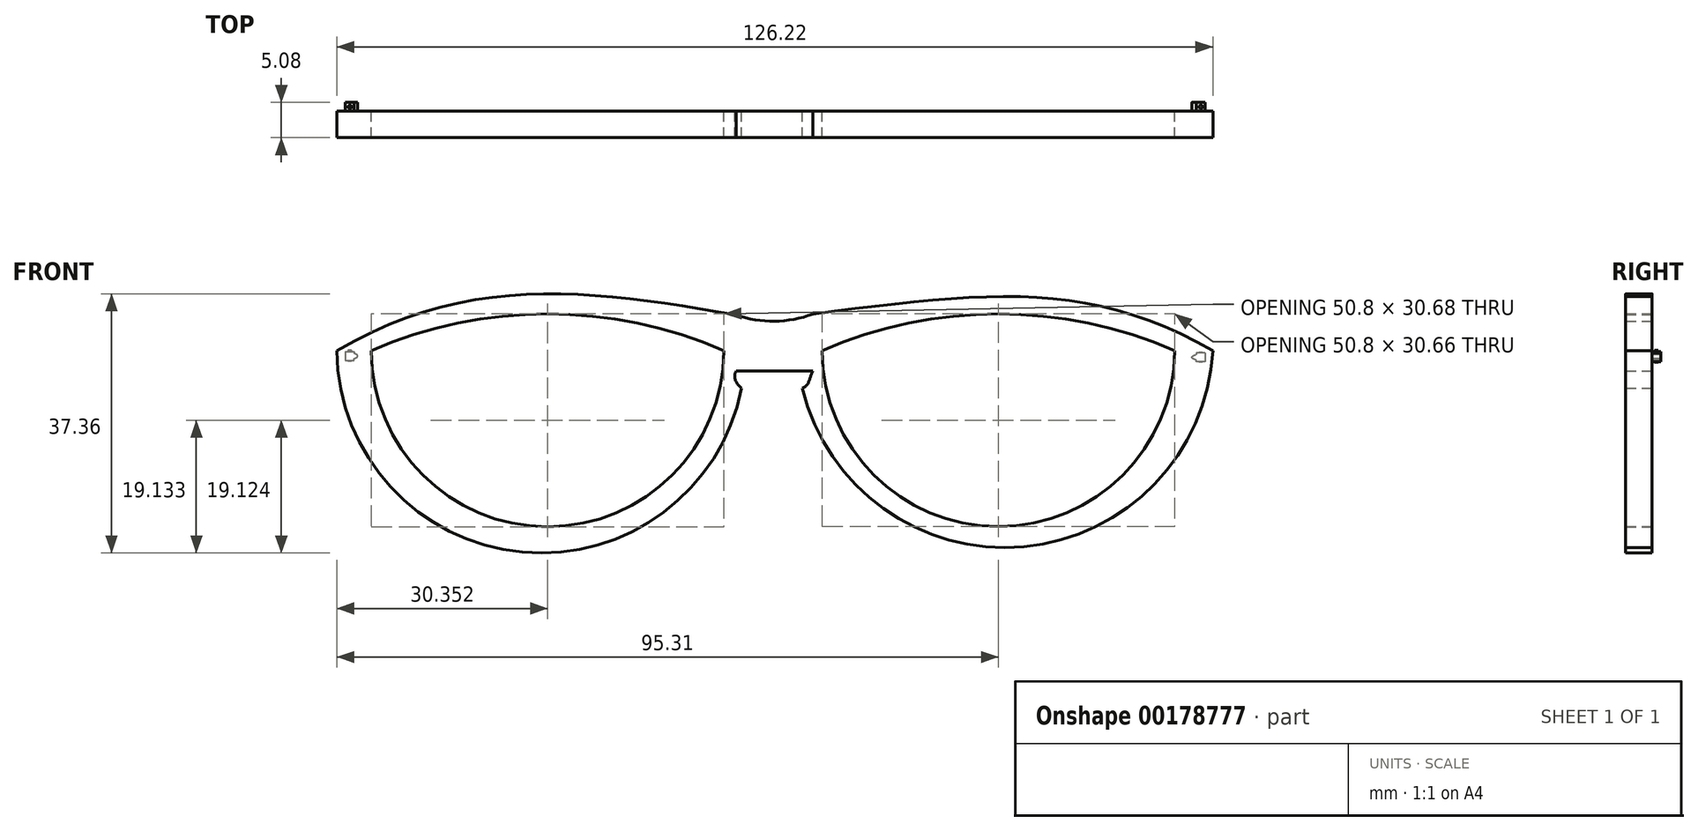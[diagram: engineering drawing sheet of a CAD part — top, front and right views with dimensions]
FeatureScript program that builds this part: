
annotation { "Feature Type Name" : "Feature", "Feature Type Description" : "" }
export const myFeature = defineFeature(function(context is Context, id is Id, definition is map)
    precondition{}
    {
        {
            var Q0;
            Q0=qCreatedBy(makeId("Front.planeOp"),FACE);
            var sketch = newSketch(context, id + "F0", { "sketchPlane" : qUnion([Q0])});
            skArc(sketch, "E0", {"start": v(-58.02, 0) * mm, "mid": v(-32.62, -25.37) * mm, "end": v(-7.22, 0) * mm});
            skArc(sketch, "E1", {"start": v(6.94, 0) * mm, "mid": v(32.34, -25.36) * mm, "end": v(57.74, 0) * mm});
            skArc(sketch, "E2", {"start": v(-7.22, 0) * mm, "mid": v(-32.62, 5.3) * mm, "end": v(-58.02, 0) * mm});
            skArc(sketch, "E3", {"start": v(57.74, 0) * mm, "mid": v(32.34, 5.3) * mm, "end": v(6.94, 0) * mm});
            skArc(sketch, "E4", {"start": v(-62.97, 0) * mm, "mid": v(-36.25, -29.04) * mm, "end": v(-4.66, -5.4) * mm});
            skArc(sketch, "E5", {"start": v(4.08, -5.4) * mm, "mid": v(36, -28.25) * mm, "end": v(63.25, 0) * mm});
            skLineSegment(sketch, "E6", {"start": v(-5.44, -2.93) * mm, "end": v(5.6, -2.93) * mm});
            skFitSpline(sketch, "E7", {"points": [v(-4.66, -5.4) * mm, v(-5.44, -2.93) * mm], "startDerivative": vector(-2.72, 1.99) * mm, "endDerivative": vector(1.48, 2.16) * mm});
            skFitSpline(sketch, "E8", {"points": [v(4.08, -5.4) * mm, v(5.6, -2.93) * mm], "startDerivative": vector(3.37, 1.04) * mm, "endDerivative": vector(1.53, 2.46) * mm});
            skArc(sketch, "E9", {"start": v(-5.44, 5.17) * mm, "mid": v(0.1, 4.25) * mm, "end": v(5.6, 5.29) * mm});
            skFitSpline(sketch, "E10", {"points": [v(-62.97, 0) * mm, v(-5.44, 5.17) * mm], "startDerivative": vector(58.46, 34.46) * mm, "endDerivative": vector(60.07, -10.18) * mm});
            skFitSpline(sketch, "E11", {"points": [v(63.25, 0) * mm, v(5.6, 5.29) * mm], "startDerivative": vector(-54.18, 31.35) * mm, "endDerivative": vector(-72.24, -9.35) * mm});
            skSolve(sketch);
        }
        {
            var Q0;
            Q0=makeQuery(id+"F0.imprint","IMPRINT",FACE,{"disambiguationData":[TD([[makeQuery(id+"F0.imprint","IMPRINT",EDGE,{"derivedFrom":sQuery(id+"F0.wireOp",EDGE,"E0")}),-1.0]])]});
            extrude(context, id + "F1", {"entities" : qUnion([Q0]), "depth" : 3.8 * mm});
        }
        {
            var Q0;
            Q0=makeQuery(id+"F1.opExtrude","CAP_FACE",FACE,{"disambiguationData":[OSD([sQuery(id+"F0.wireOp",EDGE,"E0"),sQuery(id+"F0.wireOp",EDGE,"E1"),sQuery(id+"F0.wireOp",EDGE,"E2"),sQuery(id+"F0.wireOp",EDGE,"E3"),sQuery(id+"F0.wireOp",EDGE,"E4"),sQuery(id+"F0.wireOp",EDGE,"E5"),sQuery(id+"F0.wireOp",EDGE,"E6"),sQuery(id+"F0.wireOp",EDGE,"E7"),sQuery(id+"F0.wireOp",EDGE,"E8"),sQuery(id+"F0.wireOp",EDGE,"E9"),sQuery(id+"F0.wireOp",EDGE,"E10"),sQuery(id+"F0.wireOp",EDGE,"E11")])],"isStart":true});
            var sketch = newSketch(context, id + "F2", { "sketchPlane" : qUnion([Q0])});
            skLineSegment(sketch, "E12", {"start": v(61.74, -0.13) * mm, "end": v(61.74, -1.4) * mm});
            skLineSegment(sketch, "E13", {"start": v(61.74, -1.4) * mm, "end": v(60.47, -1.4) * mm});
            skLineSegment(sketch, "E14", {"start": v(61.74, -0.13) * mm, "end": v(60.47, -0.13) * mm});
            skLineSegment(sketch, "E15", {"start": v(60.47, -1.4) * mm, "end": v(60.47, -1.15) * mm});
            skLineSegment(sketch, "E16", {"start": v(60.47, -0.13) * mm, "end": v(60.47, -0.38) * mm});
            skFitSpline(sketch, "E17", {"points": [v(60.47, -1.15) * mm, v(60.47, -0.38) * mm], "startDerivative": vector(-2.07, 0.8) * mm, "endDerivative": vector(2.02, 0.8) * mm});
            skSolve(sketch);
        }
        {
            var Q0;
            Q0=makeQuery(id+"F2.imprint","IMPRINT",FACE,{"disambiguationData":[TD([[makeQuery(id+"F2.imprint","IMPRINT",EDGE,{"derivedFrom":sQuery(id+"F2.wireOp",EDGE,"E12")}),-1.0]])]});
            extrude(context, id + "F3", {"entities" : qUnion([Q0]), "operationType" : NewBodyOperationType.ADD, "depth" : 1.27 * mm});
        }
        {
            var Q0;
            Q0=qCreatedBy(makeId("Top.planeOp"),FACE);
            var sketch = newSketch(context, id + "F4", { "sketchPlane" : qUnion([Q0])});
            skCircle(sketch, "E18", {"center": v(-61.1, 0.64) * mm, "radius": 0.25 * mm});
            skSolve(sketch);
        }
        {
            var Q0;
            Q0 = qSketchRegion(id + "F4", true);
            extrude(context, id + "F5", {"entities" : qUnion([Q0]), "depth" : 0.05 * mm});
        }
        {
            var Q0;
            Q0=makeQuery(id+"F3.opExtrude","SWEPT_FACE",FACE,{"disambiguationData":[OSD([sQuery(id+"F2.wireOp",EDGE,"E13")])]});
            var sketch = newSketch(context, id + "F6", { "sketchPlane" : qUnion([Q0])});
            skCircle(sketch, "E19", {"center": v(-61.1, -0.64) * mm, "radius": 0.25 * mm});
            skSolve(sketch);
        }
        {
            var Q0;
            Q0 = qSketchRegion(id + "F6", true);
            extrude(context, id + "F7", {"entities" : qUnion([Q0]), "operationType" : NewBodyOperationType.ADD, "depth" : 0.05 * mm});
        }
        {
            var Q0;
            Q0=makeQuery(id+"F1.opExtrude","CAP_FACE",FACE,{"disambiguationData":[OSD([sQuery(id+"F0.wireOp",EDGE,"E0"),sQuery(id+"F0.wireOp",EDGE,"E1"),sQuery(id+"F0.wireOp",EDGE,"E2"),sQuery(id+"F0.wireOp",EDGE,"E3"),sQuery(id+"F0.wireOp",EDGE,"E4"),sQuery(id+"F0.wireOp",EDGE,"E5"),sQuery(id+"F0.wireOp",EDGE,"E6"),sQuery(id+"F0.wireOp",EDGE,"E7"),sQuery(id+"F0.wireOp",EDGE,"E8"),sQuery(id+"F0.wireOp",EDGE,"E9"),sQuery(id+"F0.wireOp",EDGE,"E10"),sQuery(id+"F0.wireOp",EDGE,"E11")])],"isStart":true});
            var sketch = newSketch(context, id + "F8", { "sketchPlane" : qUnion([Q0])});
            skSolve(sketch);
        }
        {
            var Q0;
            Q0=makeQuery(id+"F8.imprint","IMPRINT",FACE,{"disambiguationData":[TD([[makeQuery(id+"F8.imprint","IMPRINT",EDGE,{"derivedFrom":makeQuery(id+"F1.opExtrude","CAP_EDGE",EDGE,{"disambiguationData":[OSD([sQuery(id+"F0.wireOp",EDGE,"E0")])],"isStart":true})}),1.0]])]});
            var sketch = newSketch(context, id + "F9", { "sketchPlane" : qUnion([Q0])});
            skLineSegment(sketch, "E20", {"start": v(-62.14, -0.32) * mm, "end": v(-60.87, -0.32) * mm});
            skLineSegment(sketch, "E21", {"start": v(-62.14, -0.32) * mm, "end": v(-62.14, -1.6) * mm});
            skLineSegment(sketch, "E22", {"start": v(-62.14, -1.6) * mm, "end": v(-60.87, -1.6) * mm});
            skLineSegment(sketch, "E23", {"start": v(-60.87, -1.6) * mm, "end": v(-60.87, -1.34) * mm});
            skLineSegment(sketch, "E24", {"start": v(-60.87, -0.32) * mm, "end": v(-60.87, -0.58) * mm});
            skFitSpline(sketch, "E25", {"points": [v(-60.87, -1.34) * mm, v(-60.87, -0.58) * mm], "startDerivative": vector(2.46, 0.55) * mm, "endDerivative": vector(-2.8, 0.69) * mm});
            skSolve(sketch);
        }
        {
            var Q0;
            Q0 = qSketchRegion(id + "F9", true);
            extrude(context, id + "F10", {"entities" : qUnion([Q0]), "operationType" : NewBodyOperationType.ADD, "depth" : 1.27 * mm});
        }
        {
            var Q0;
            Q0=makeQuery(id+"F10.opExtrude","SWEPT_FACE",FACE,{"disambiguationData":[OSD([sQuery(id+"F9.wireOp",EDGE,"E22")])]});
            var sketch = newSketch(context, id + "F11", { "sketchPlane" : qUnion([Q0])});
            skCircle(sketch, "E26", {"center": v(61.5, -0.64) * mm, "radius": 0.25 * mm});
            skSolve(sketch);
        }
        {
            var Q0;
            Q0 = qSketchRegion(id + "F11", true);
            extrude(context, id + "F12", {"entities" : qUnion([Q0]), "operationType" : NewBodyOperationType.ADD, "depth" : 0.05 * mm});
        }
        {
            var Q0;
            Q0=makeQuery(id+"F10.opExtrude","SWEPT_FACE",FACE,{"disambiguationData":[OSD([sQuery(id+"F9.wireOp",EDGE,"E20")])]});
            var sketch = newSketch(context, id + "F13", { "sketchPlane" : qUnion([Q0])});
            skCircle(sketch, "E27", {"center": v(61.5, 0.64) * mm, "radius": 0.25 * mm});
            skSolve(sketch);
        }
        {
            var Q0;
            Q0 = qSketchRegion(id + "F13", true);
            extrude(context, id + "F14", {"entities" : qUnion([Q0]), "operationType" : NewBodyOperationType.ADD, "depth" : 0.05 * mm});
        }
    });
